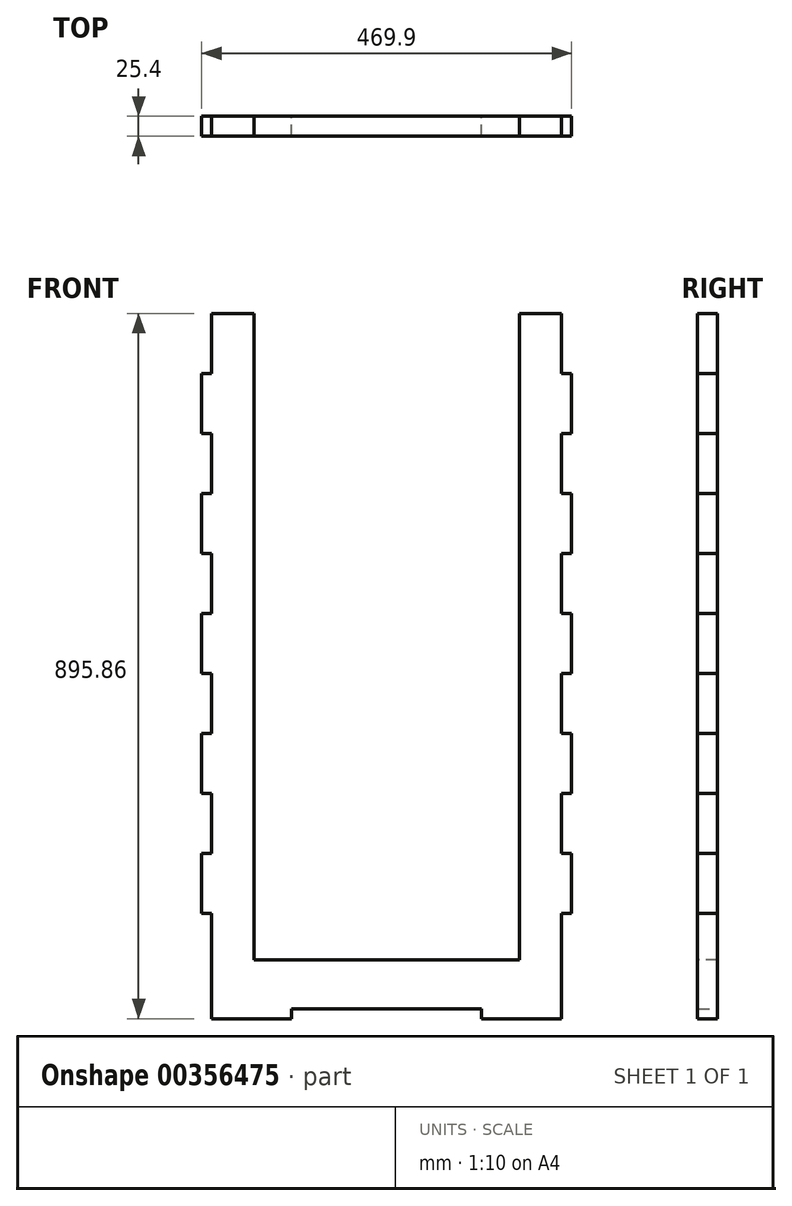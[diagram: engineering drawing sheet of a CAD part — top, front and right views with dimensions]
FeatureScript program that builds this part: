
annotation { "Feature Type Name" : "Feature", "Feature Type Description" : "" }
export const myFeature = defineFeature(function(context is Context, id is Id, definition is map)
    precondition{}
    {
        {
            var Q0;
            Q0=qCreatedBy(makeId("Front.planeOp"),FACE);
            var sketch = newSketch(context, id + "F0", { "sketchPlane" : qUnion([Q0])});
            skLineSegment(sketch, "E0", {"start": v(128.93, 183.28) * mm, "end": v(-93.32, 183.28) * mm});
            skLineSegment(sketch, "E1.top", {"start": v(-93.32, 107.08) * mm, "end": v(-106.02, 107.08) * mm});
            skLineSegment(sketch, "E2.bottom", {"start": v(-106.02, 30.88) * mm, "end": v(-93.32, 30.88) * mm});
            skLineSegment(sketch, "E2.top", {"start": v(-106.02, -45.32) * mm, "end": v(-93.32, -45.32) * mm});
            skLineSegment(sketch, "E3.MirrorCS", {"start": v(-106.02, -197.72) * mm, "end": v(-93.32, -197.72) * mm});
            skLineSegment(sketch, "E4.MirrorCS", {"start": v(-106.02, -578.72) * mm, "end": v(-93.32, -578.72) * mm});
            skLineSegment(sketch, "E5.MirrorCS", {"start": v(-106.02, -350.12) * mm, "end": v(-93.32, -350.12) * mm});
            skLineSegment(sketch, "E6.MirrorCS", {"start": v(-106.02, -502.52) * mm, "end": v(-93.32, -502.52) * mm});
            skLineSegment(sketch, "E7.MirrorCS", {"start": v(-106.02, -426.32) * mm, "end": v(-93.32, -426.32) * mm});
            skLineSegment(sketch, "E8.MirrorCS", {"start": v(-106.02, -121.52) * mm, "end": v(-93.32, -121.52) * mm});
            skLineSegment(sketch, "E9.MirrorCS", {"start": v(-106.02, -273.92) * mm, "end": v(-93.32, -273.92) * mm});
            skPoint(sketch, "E10.end.orphan", {"position": v(128.93, -699.88) * mm});
            skLineSegment(sketch, "E11", {"start": v(-106.02, 30.88) * mm, "end": v(-106.02, 107.08) * mm});
            skLineSegment(sketch, "E12", {"start": v(-93.32, 107.08) * mm, "end": v(-93.32, 183.28) * mm});
            skLineSegment(sketch, "E13", {"start": v(-93.32, 30.88) * mm, "end": v(-93.32, -45.32) * mm});
            skLineSegment(sketch, "E14", {"start": v(-106.02, -45.32) * mm, "end": v(-106.02, -121.52) * mm});
            skLineSegment(sketch, "E15", {"start": v(-93.32, -121.52) * mm, "end": v(-93.32, -197.72) * mm});
            skLineSegment(sketch, "E16", {"start": v(-106.02, -197.72) * mm, "end": v(-106.02, -273.92) * mm});
            skLineSegment(sketch, "E17", {"start": v(-93.32, -273.92) * mm, "end": v(-93.32, -350.12) * mm});
            skLineSegment(sketch, "E18", {"start": v(-106.02, -350.12) * mm, "end": v(-106.02, -426.32) * mm});
            skLineSegment(sketch, "E19", {"start": v(-106.02, -502.52) * mm, "end": v(-106.02, -578.72) * mm});
            skLineSegment(sketch, "E20", {"start": v(-93.32, -502.52) * mm, "end": v(-93.32, -426.32) * mm});
            skLineSegment(sketch, "E21", {"start": v(-93.32, -578.72) * mm, "end": v(-93.32, -699.88) * mm});
            skLineSegment(sketch, "E22", {"start": v(128.93, 183.28) * mm, "end": v(128.93, -699.88) * mm});
            skLineSegment(sketch, "E23", {"start": v(128.93, -699.88) * mm, "end": v(-93.32, -699.88) * mm});
            skLineSegment(sketch, "E24.MirrorCS", {"start": v(363.88, -45.32) * mm, "end": v(351.18, -45.32) * mm});
            skLineSegment(sketch, "E25.MirrorCS", {"start": v(363.88, 30.88) * mm, "end": v(351.18, 30.88) * mm});
            skLineSegment(sketch, "E26.MirrorCS", {"start": v(351.18, 107.08) * mm, "end": v(363.88, 107.08) * mm});
            skLineSegment(sketch, "E27.MirrorCS", {"start": v(363.88, -426.32) * mm, "end": v(351.18, -426.32) * mm});
            skLineSegment(sketch, "E28.MirrorCS", {"start": v(363.88, -502.52) * mm, "end": v(351.18, -502.52) * mm});
            skLineSegment(sketch, "E29.MirrorCS", {"start": v(363.88, -578.72) * mm, "end": v(351.18, -578.72) * mm});
            skLineSegment(sketch, "E30.MirrorCS", {"start": v(363.88, -121.52) * mm, "end": v(351.18, -121.52) * mm});
            skLineSegment(sketch, "E31.MirrorCS", {"start": v(363.88, -197.72) * mm, "end": v(351.18, -197.72) * mm});
            skLineSegment(sketch, "E32.MirrorCS", {"start": v(363.88, -350.12) * mm, "end": v(351.18, -350.12) * mm});
            skLineSegment(sketch, "E33.MirrorCS", {"start": v(363.88, -273.92) * mm, "end": v(351.18, -273.92) * mm});
            skLineSegment(sketch, "E34.MirrorCS", {"start": v(351.18, -502.52) * mm, "end": v(351.18, -426.32) * mm});
            skLineSegment(sketch, "E35.MirrorCS", {"start": v(351.18, -273.92) * mm, "end": v(351.18, -350.12) * mm});
            skLineSegment(sketch, "E36.MirrorCS", {"start": v(351.18, 107.08) * mm, "end": v(351.18, 183.28) * mm});
            skLineSegment(sketch, "E37.MirrorCS", {"start": v(363.88, -502.52) * mm, "end": v(363.88, -578.72) * mm});
            skLineSegment(sketch, "E38.MirrorCS", {"start": v(363.88, -350.12) * mm, "end": v(363.88, -426.32) * mm});
            skLineSegment(sketch, "E39.MirrorCS", {"start": v(351.18, 30.88) * mm, "end": v(351.18, -45.32) * mm});
            skLineSegment(sketch, "E40.MirrorCS", {"start": v(363.88, -45.32) * mm, "end": v(363.88, -121.52) * mm});
            skLineSegment(sketch, "E41.MirrorCS", {"start": v(363.88, -197.72) * mm, "end": v(363.88, -273.92) * mm});
            skLineSegment(sketch, "E42.MirrorCS", {"start": v(363.88, 30.88) * mm, "end": v(363.88, 107.08) * mm});
            skLineSegment(sketch, "E43.MirrorCS", {"start": v(351.18, -121.52) * mm, "end": v(351.18, -197.72) * mm});
            skLineSegment(sketch, "E44.MirrorCS", {"start": v(351.18, -578.72) * mm, "end": v(351.18, -699.88) * mm});
            skLineSegment(sketch, "E45.MirrorCS", {"start": v(128.93, 183.28) * mm, "end": v(351.18, 183.28) * mm});
            skLineSegment(sketch, "E46.MirrorCS", {"start": v(128.93, -699.88) * mm, "end": v(351.18, -699.88) * mm});
            skLineSegment(sketch, "E47.bottom", {"start": v(351.18, -699.88) * mm, "end": v(249.58, -699.88) * mm});
            skLineSegment(sketch, "E47.top", {"start": v(351.18, -712.58) * mm, "end": v(249.58, -712.58) * mm});
            skLineSegment(sketch, "E47.left", {"start": v(351.18, -699.88) * mm, "end": v(351.18, -712.58) * mm});
            skLineSegment(sketch, "E47.right", {"start": v(249.58, -699.88) * mm, "end": v(249.58, -712.58) * mm});
            skLineSegment(sketch, "E48.top", {"start": v(249.58, -699.88) * mm, "end": v(-93.32, -699.88) * mm});
            skLineSegment(sketch, "E48.left", {"start": v(249.58, -712.58) * mm, "end": v(249.58, -699.88) * mm});
            skLineSegment(sketch, "E49.bottom", {"start": v(8.28, -712.58) * mm, "end": v(-93.32, -712.58) * mm});
            skLineSegment(sketch, "E49.top", {"start": v(8.28, -699.88) * mm, "end": v(-93.32, -699.88) * mm});
            skLineSegment(sketch, "E49.left", {"start": v(8.28, -712.58) * mm, "end": v(8.28, -699.88) * mm});
            skLineSegment(sketch, "E49.right", {"start": v(-93.32, -712.58) * mm, "end": v(-93.32, -699.88) * mm});
            skSolve(sketch);
        }
        {
            var Q0;
            Q0 = qSketchRegion(id + "F0", true);
            extrude(context, id + "F1", {"entities" : qUnion([Q0]), "depth" : 25.4 * mm});
        }
        {
            var Q0;
            Q0=makeQuery(id+"F1.opExtrude","CAP_FACE",FACE,{"disambiguationData":[OSD([sQuery(id+"F0.wireOp",EDGE,"E0"),sQuery(id+"F0.wireOp",EDGE,"E3.MirrorCS"),sQuery(id+"F0.wireOp",EDGE,"E4.MirrorCS"),sQuery(id+"F0.wireOp",EDGE,"E2.bottom"),sQuery(id+"F0.wireOp",EDGE,"E5.MirrorCS"),sQuery(id+"F0.wireOp",EDGE,"E6.MirrorCS"),sQuery(id+"F0.wireOp",EDGE,"E7.MirrorCS"),sQuery(id+"F0.wireOp",EDGE,"E8.MirrorCS"),sQuery(id+"F0.wireOp",EDGE,"E1.top"),sQuery(id+"F0.wireOp",EDGE,"E2.top"),sQuery(id+"F0.wireOp",EDGE,"E9.MirrorCS"),sQuery(id+"F0.wireOp",EDGE,"E11"),sQuery(id+"F0.wireOp",EDGE,"E12"),sQuery(id+"F0.wireOp",EDGE,"E13"),sQuery(id+"F0.wireOp",EDGE,"E14"),sQuery(id+"F0.wireOp",EDGE,"E15"),sQuery(id+"F0.wireOp",EDGE,"E16"),sQuery(id+"F0.wireOp",EDGE,"E17"),sQuery(id+"F0.wireOp",EDGE,"E18"),sQuery(id+"F0.wireOp",EDGE,"E19"),sQuery(id+"F0.wireOp",EDGE,"E20"),sQuery(id+"F0.wireOp",EDGE,"E21"),sQuery(id+"F0.wireOp",EDGE,"E25.MirrorCS"),sQuery(id+"F0.wireOp",EDGE,"E26.MirrorCS"),sQuery(id+"F0.wireOp",EDGE,"E24.MirrorCS"),sQuery(id+"F0.wireOp",EDGE,"E27.MirrorCS"),sQuery(id+"F0.wireOp",EDGE,"E28.MirrorCS"),sQuery(id+"F0.wireOp",EDGE,"E29.MirrorCS"),sQuery(id+"F0.wireOp",EDGE,"E30.MirrorCS"),sQuery(id+"F0.wireOp",EDGE,"E31.MirrorCS"),sQuery(id+"F0.wireOp",EDGE,"E32.MirrorCS"),sQuery(id+"F0.wireOp",EDGE,"E33.MirrorCS"),sQuery(id+"F0.wireOp",EDGE,"E34.MirrorCS"),sQuery(id+"F0.wireOp",EDGE,"E35.MirrorCS"),sQuery(id+"F0.wireOp",EDGE,"E36.MirrorCS"),sQuery(id+"F0.wireOp",EDGE,"E37.MirrorCS"),sQuery(id+"F0.wireOp",EDGE,"E38.MirrorCS"),sQuery(id+"F0.wireOp",EDGE,"E39.MirrorCS"),sQuery(id+"F0.wireOp",EDGE,"E40.MirrorCS"),sQuery(id+"F0.wireOp",EDGE,"E41.MirrorCS"),sQuery(id+"F0.wireOp",EDGE,"E42.MirrorCS"),sQuery(id+"F0.wireOp",EDGE,"E43.MirrorCS"),sQuery(id+"F0.wireOp",EDGE,"E44.MirrorCS"),sQuery(id+"F0.wireOp",EDGE,"E45.MirrorCS"),sQuery(id+"F0.wireOp",EDGE,"E47.top"),sQuery(id+"F0.wireOp",EDGE,"E47.left"),sQuery(id+"F0.wireOp",EDGE,"E48.top"),sQuery(id+"F0.wireOp",EDGE,"E48.left"),sQuery(id+"F0.wireOp",EDGE,"E49.bottom"),sQuery(id+"F0.wireOp",EDGE,"E49.left"),sQuery(id+"F0.wireOp",EDGE,"E49.right")])],"isStart":false});
            var sketch = newSketch(context, id + "F2", { "sketchPlane" : qUnion([Q0])});
            skLineSegment(sketch, "E50.0", {"start": v(128.93, 183.28) * mm, "end": v(128.93, -699.88) * mm});
            skLineSegment(sketch, "E51.bottom", {"start": v(297.58, 121.35) * mm, "end": v(-39.72, 121.35) * mm});
            skLineSegment(sketch, "E51.top", {"start": v(297.58, -637.95) * mm, "end": v(-39.72, -637.95) * mm});
            skLineSegment(sketch, "E51.left", {"start": v(297.58, 121.35) * mm, "end": v(297.58, -637.95) * mm});
            skLineSegment(sketch, "E51.right", {"start": v(-39.72, 121.35) * mm, "end": v(-39.72, -637.95) * mm});
            skPoint(sketch, "E51.middle", {"position": v(128.93, -258.3) * mm});
            skLineSegment(sketch, "E52.bottom", {"start": v(-39.72, 121.35) * mm, "end": v(297.58, 121.35) * mm});
            skLineSegment(sketch, "E52.top", {"start": v(-39.72, 183.28) * mm, "end": v(297.58, 183.28) * mm});
            skLineSegment(sketch, "E52.left", {"start": v(-39.72, 121.35) * mm, "end": v(-39.72, 183.28) * mm});
            skLineSegment(sketch, "E52.right", {"start": v(297.58, 121.35) * mm, "end": v(297.58, 183.28) * mm});
            skSolve(sketch);
        }
        {
            var Q0;
            Q0 = qSketchRegion(id + "F2", true);
            extrude(context, id + "F3", {"entities" : qUnion([Q0]), "operationType" : NewBodyOperationType.REMOVE, "endBound" : BoundingType.THROUGH_ALL, "oppositeDirection" : true, "depth" : 25.4 * mm});
        }
    });
